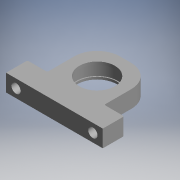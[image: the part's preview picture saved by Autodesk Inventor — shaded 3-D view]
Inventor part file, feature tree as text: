
AUTODESK INVENTOR PART (.ipt)
format: ipt  version: 2017.3 (Build 213256000, 256)  size: 142,848 bytes
history: native  units: mm (DEFAULTED — no unit token found)
features: other x14, sketch x3, extrude x1, revolve x1, hole x1, pattern_linear x1
ambient origin geometry x8: Origin, YZ Plane, XZ Plane, XY Plane, X Axis, Y Axis, Z Axis, Center Point
bodies: Solid1 (feature_tree)
feature tree (21):
  extrude  "Extrusion1"  TaperAngle=360.0deg  [1 undecoded]
  revolve  "Revolution1"  [1 undecoded]
  hole  "Hole1"  [1 undecoded]
  pattern_linear  "Rectangular Pattern1"  [2 undecoded]
  other  "to_bearing_XY"
  other  "to_bearing_YZ"
  other  "to_bearing_ZX"
  other  "to_bearing_X"
  other  "to_bearing_Y"
  other  "to_bearing_Z"
  other  "to_bearing_Center"
  other  "to_snapring_XY"
  other  "to_snapring_YZ"
  other  "to_snapring_ZX"
  other  "to_snapring_X"
  other  "to_snapring_Y"
  other  "to_snapring_Z"
  other  "to_snapring_Center"
  sketch  "Sketch_1"  dims[d0=12.0mm d1=0.0mm d2=360.0deg]
  sketch  "Sketch_2"  dims[d3=6.5mm d4=6.0mm d5=4.0mm d6=2.0mm d7=90.0deg d8=15.0mm d9=0.0mm d10=20.0mm d12=54.0mm d13=10.0mm d15=0.0mm]
  sketch  "Sketch3"  dims[d16=0.0mm d17=0.0mm]
note: 5 required parameter values undecoded (feature->parameter linkage not recoverable at this tier; creation-order binding heuristic only, values carry confidence <= 0.55)